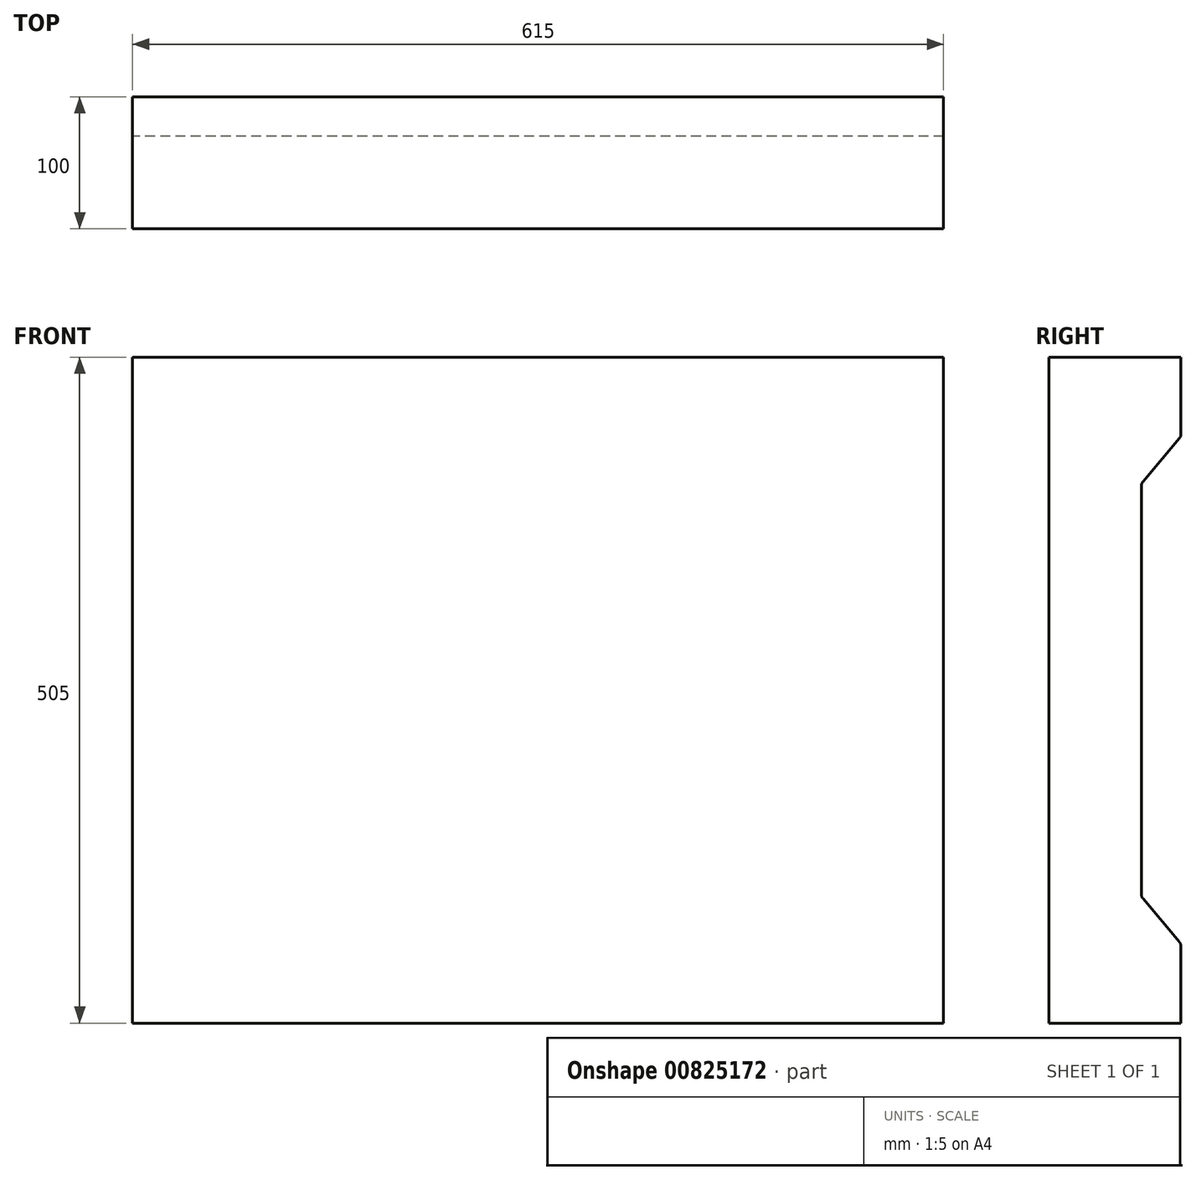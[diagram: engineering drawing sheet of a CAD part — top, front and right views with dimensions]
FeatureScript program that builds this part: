
annotation { "Feature Type Name" : "Feature", "Feature Type Description" : "" }
export const myFeature = defineFeature(function(context is Context, id is Id, definition is map)
    precondition{}
    {
        {
            var Q0;
            Q0=qCreatedBy(makeId("Right.planeOp"),FACE);
            var sketch = newSketch(context, id + "F0", { "sketchPlane" : qUnion([Q0])});
            skLineSegment(sketch, "E0", {"start": v(14.21, -112.43) * mm, "end": v(114.21, -112.43) * mm});
            skLineSegment(sketch, "E1", {"start": v(114.21, -112.43) * mm, "end": v(114.21, -52.43) * mm});
            skLineSegment(sketch, "E2", {"start": v(114.21, -52.43) * mm, "end": v(84.21, -16.68) * mm});
            skLineSegment(sketch, "E3", {"start": v(84.21, -16.68) * mm, "end": v(84.21, 296.81) * mm});
            skLineSegment(sketch, "E4", {"start": v(84.21, 296.81) * mm, "end": v(114.21, 332.57) * mm});
            skLineSegment(sketch, "E5", {"start": v(114.21, 332.57) * mm, "end": v(114.21, 392.57) * mm});
            skLineSegment(sketch, "E6", {"start": v(114.21, 392.57) * mm, "end": v(14.21, 392.57) * mm});
            skLineSegment(sketch, "E7", {"start": v(14.21, 392.57) * mm, "end": v(14.21, -112.43) * mm});
            skSolve(sketch);
        }
        {
            var Q0;
            Q0=makeQuery(id+"F0.imprint","IMPRINT",FACE,{"disambiguationData":[TD([[makeQuery(id+"F0.imprint","IMPRINT",EDGE,{"derivedFrom":sQuery(id+"F0.wireOp",EDGE,"E0")}),1.0]])]});
            extrude(context, id + "F1", {"entities" : qUnion([Q0]), "endBound" : BoundingType.SYMMETRIC, "depth" : 615 * mm, "offsetDistance" : 25 * mm});
        }
        {
            var Q0;
            Q0=makeQuery(id+"F1.opExtrude","SWEPT_EDGE",EDGE,{"disambiguationData":[OSD([sQuery(id+"F0.wireOp",EDGE,"E1"),sQuery(id+"F0.wireOp",EDGE,"E2")])]});
            var Q1;
            Q1=makeQuery(id+"F1.opExtrude","SWEPT_EDGE",EDGE,{"disambiguationData":[OSD([sQuery(id+"F0.wireOp",EDGE,"E2"),sQuery(id+"F0.wireOp",EDGE,"E3")])]});
            var Q2;
            Q2=makeQuery(id+"F1.opExtrude","SWEPT_EDGE",EDGE,{"disambiguationData":[OSD([sQuery(id+"F0.wireOp",EDGE,"E3"),sQuery(id+"F0.wireOp",EDGE,"E4")])]});
            var Q3;
            Q3=makeQuery(id+"F1.opExtrude","SWEPT_EDGE",EDGE,{"disambiguationData":[OSD([sQuery(id+"F0.wireOp",EDGE,"E4"),sQuery(id+"F0.wireOp",EDGE,"E5")])]});
            fillet(context, id + "F2", {"entities" : qUnion([Q0, Q1, Q2, Q3]), "radius" : 5 * mm, "tangentPropagation" : true, "allowEdgeOverflow" : false});
        }
    });
